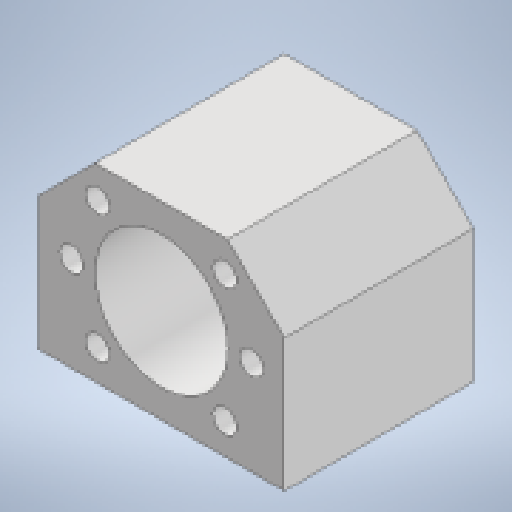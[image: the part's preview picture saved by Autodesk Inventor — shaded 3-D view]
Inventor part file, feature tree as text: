
AUTODESK INVENTOR PART (.ipt)
format: ipt  version: 2023 (Build 270158000, 158)  size: 157,696 bytes
history: native  units: mm
features: extrude x2, sketch x2
ambient origin geometry x8: Origin, YZ Plane, XZ Plane, XY Plane, X Axis, Y Axis, Z Axis, Center Point
bodies: Solid1 (feature_tree)
feature tree (4):
  extrude  "Extrusion1"  Depth=40.0mm
  extrude  "Extrusion2"  Depth=10.0mm
  sketch  "Sketch1"  dims[d0=28.0mm d1=40.0mm]
  sketch  "Sketch2"  dims[d2=52.0mm d3=38.0mm d4=5.0mm d5=45.0deg d6=20.0mm d7=135.0deg d8=12.0mm d9=40.0mm d10=0.0mm d11=5.0mm d12=40.0mm d13=24.0mm d14=10.0mm d15=0.0mm]
